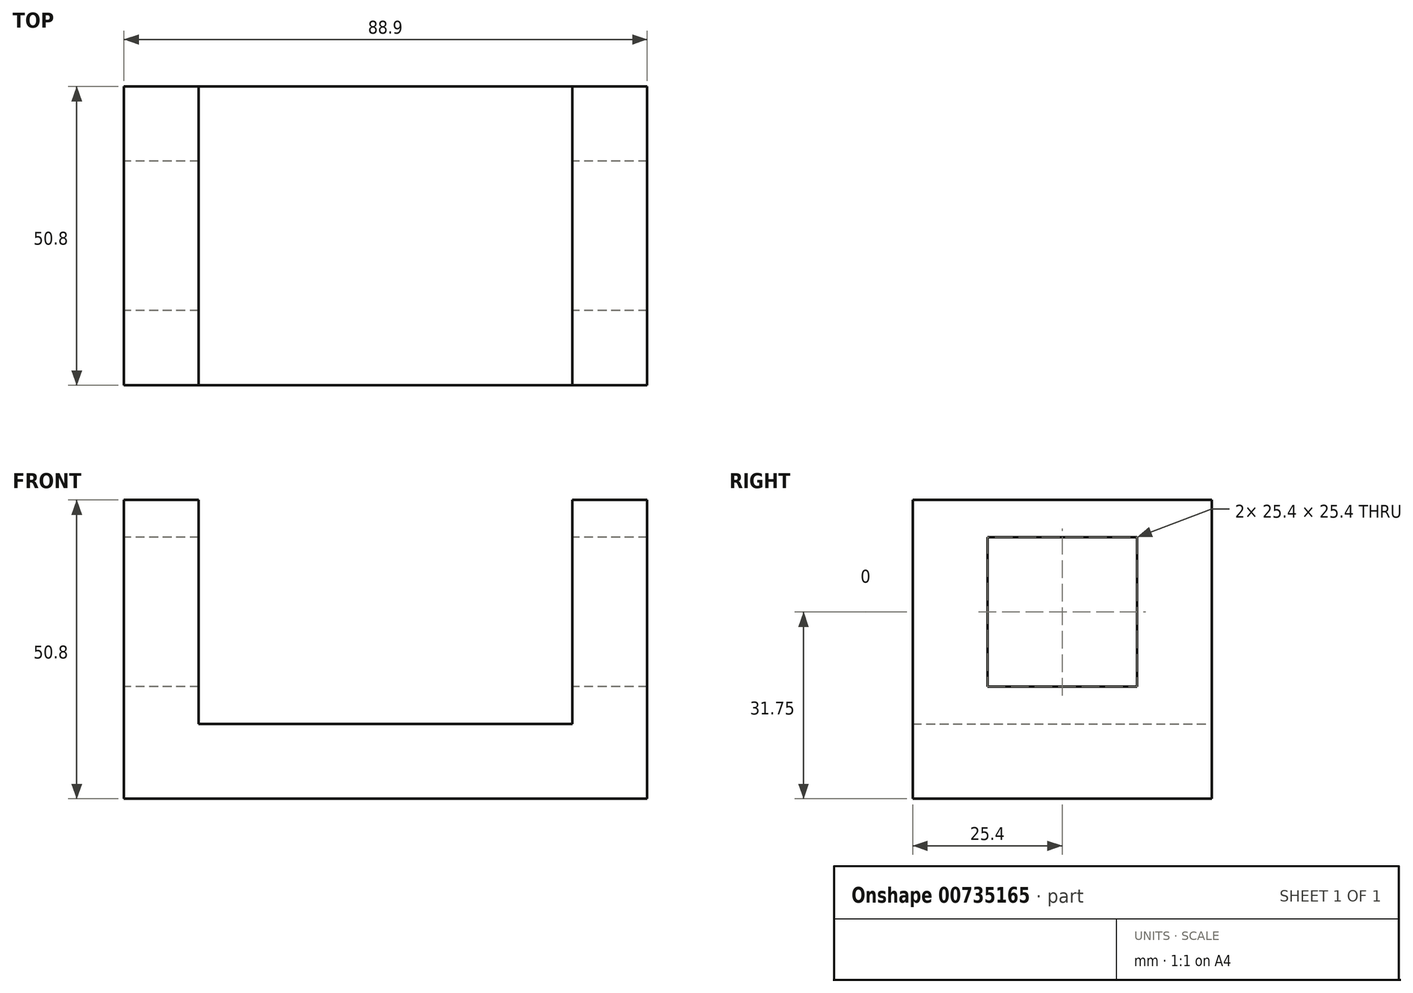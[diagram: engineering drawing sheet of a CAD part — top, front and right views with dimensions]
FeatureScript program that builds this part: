
annotation { "Feature Type Name" : "Feature", "Feature Type Description" : "" }
export const myFeature = defineFeature(function(context is Context, id is Id, definition is map)
    precondition{}
    {
        {
            var Q0;
            Q0=qCreatedBy(makeId("Front.planeOp"),FACE);
            var sketch = newSketch(context, id + "F0", { "sketchPlane" : qUnion([Q0])});
            skLineSegment(sketch, "E0", {"start": v(-33.6, 34.17) * mm, "end": v(-33.6, -16.63) * mm});
            skLineSegment(sketch, "E1", {"start": v(-33.6, -16.63) * mm, "end": v(55.3, -16.63) * mm});
            skLineSegment(sketch, "E2", {"start": v(55.3, -16.63) * mm, "end": v(55.3, 34.17) * mm});
            skLineSegment(sketch, "E3", {"start": v(-33.6, 34.17) * mm, "end": v(-20.9, 34.17) * mm});
            skLineSegment(sketch, "E4", {"start": v(-20.9, 34.17) * mm, "end": v(-20.9, -3.93) * mm});
            skLineSegment(sketch, "E5", {"start": v(55.3, 34.17) * mm, "end": v(42.6, 34.17) * mm});
            skLineSegment(sketch, "E6", {"start": v(-20.9, -3.93) * mm, "end": v(42.6, -3.93) * mm});
            skLineSegment(sketch, "E7", {"start": v(42.6, 34.17) * mm, "end": v(42.6, -3.93) * mm});
            skSolve(sketch);
        }
        {
            var Q0;
            Q0 = qSketchRegion(id + "F0", true);
            extrude(context, id + "F1", {"entities" : qUnion([Q0]), "depth" : 50.8 * mm, "offsetDistance" : 25.4 * mm});
        }
        {
            var Q0;
            Q0=makeQuery(id+"F1.opExtrude","SWEPT_FACE",FACE,{"disambiguationData":[OSD([sQuery(id+"F0.wireOp",EDGE,"E0")])]});
            var sketch = newSketch(context, id + "F2", { "sketchPlane" : qUnion([Q0])});
            skLineSegment(sketch, "E8", {"start": v(12.7, 27.82) * mm, "end": v(38.1, 27.82) * mm});
            skLineSegment(sketch, "E9", {"start": v(38.1, 27.82) * mm, "end": v(38.1, 2.42) * mm});
            skLineSegment(sketch, "E10", {"start": v(38.1, 2.42) * mm, "end": v(12.7, 2.42) * mm});
            skLineSegment(sketch, "E11", {"start": v(12.7, 2.42) * mm, "end": v(12.7, 27.82) * mm});
            skSolve(sketch);
        }
        {
            var Q0;
            Q0=makeQuery(id+"F2.imprint","IMPRINT",FACE,{"disambiguationData":[TD([[makeQuery(id+"F2.imprint","IMPRINT",EDGE,{"derivedFrom":sQuery(id+"F2.wireOp",EDGE,"E8")}),-1.0]])]});
            extrude(context, id + "F3", {"entities" : qUnion([Q0]), "operationType" : NewBodyOperationType.REMOVE, "oppositeDirection" : true, "depth" : 12.7 * mm, "offsetDistance" : 25.4 * mm});
        }
        {
            var Q0;
            Q0=makeQuery(id+"F1.opExtrude","SWEPT_FACE",FACE,{"disambiguationData":[OSD([sQuery(id+"F0.wireOp",EDGE,"E7")])]});
            var sketch = newSketch(context, id + "F4", { "sketchPlane" : qUnion([Q0])});
            skLineSegment(sketch, "E12", {"start": v(38.1, 27.82) * mm, "end": v(12.7, 27.82) * mm});
            skLineSegment(sketch, "E13", {"start": v(12.7, 27.82) * mm, "end": v(12.7, 2.42) * mm});
            skLineSegment(sketch, "E14", {"start": v(12.7, 2.42) * mm, "end": v(38.1, 2.42) * mm});
            skLineSegment(sketch, "E15", {"start": v(38.1, 27.82) * mm, "end": v(38.1, 2.42) * mm});
            skSolve(sketch);
        }
        {
            var Q0;
            Q0 = qSketchRegion(id + "F4", true);
            extrude(context, id + "F5", {"entities" : qUnion([Q0]), "operationType" : NewBodyOperationType.REMOVE, "oppositeDirection" : true, "depth" : 12.7 * mm, "offsetDistance" : 25.4 * mm});
        }
        {
            var Q0;
            Q0 = qSketchRegion(id + "F2", true);
            extrude(context, id + "F6", {"entities" : qUnion([Q0]), "operationType" : NewBodyOperationType.REMOVE, "oppositeDirection" : true, "depth" : 12.7 * mm, "offsetDistance" : 25.4 * mm});
        }
    });
